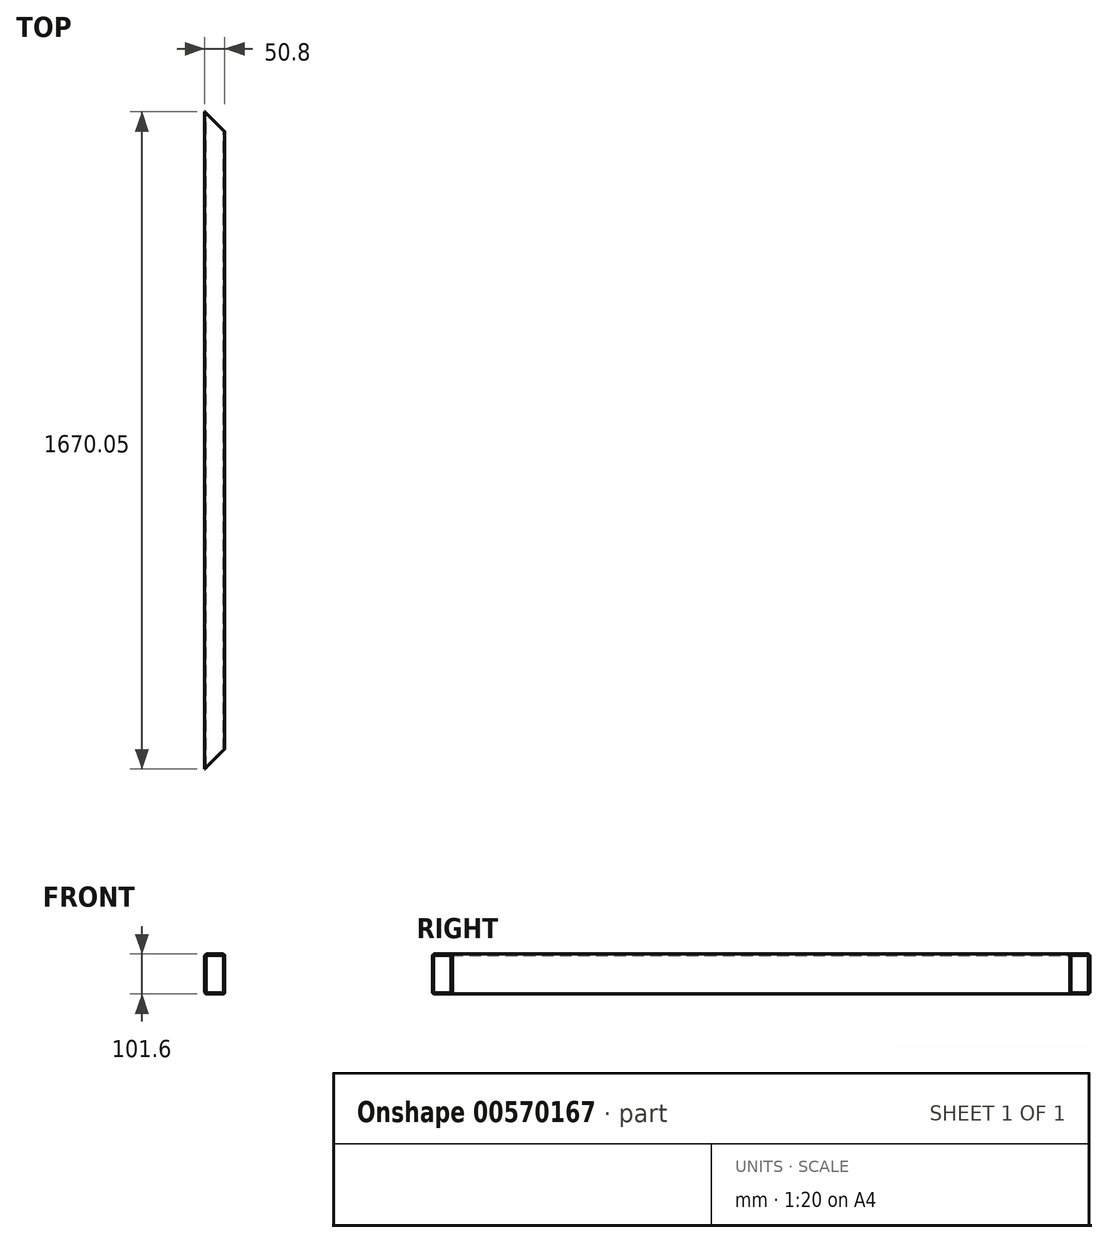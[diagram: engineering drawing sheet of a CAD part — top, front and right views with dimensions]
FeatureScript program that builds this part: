
annotation { "Feature Type Name" : "Feature", "Feature Type Description" : "" }
export const myFeature = defineFeature(function(context is Context, id is Id, definition is map)
    precondition{}
    {
        {
            var Q0;
            Q0=qCreatedBy(makeId("Front.planeOp"),FACE);
            var sketch = newSketch(context, id + "F0", { "sketchPlane" : qUnion([Q0])});
            skLineSegment(sketch, "E0.bottom", {"start": v(0, 0) * mm, "end": v(50.8, 0) * mm});
            skLineSegment(sketch, "E0.top", {"start": v(0, 101.6) * mm, "end": v(50.8, 101.6) * mm});
            skLineSegment(sketch, "E0.left", {"start": v(0, 0) * mm, "end": v(0, 101.6) * mm});
            skLineSegment(sketch, "E0.right", {"start": v(50.8, 0) * mm, "end": v(50.8, 101.6) * mm});
            skLineSegment(sketch, "E1.bottom", {"start": v(3.17, 3.18) * mm, "end": v(47.62, 3.18) * mm});
            skLineSegment(sketch, "E1.top", {"start": v(3.17, 98.43) * mm, "end": v(47.62, 98.43) * mm});
            skLineSegment(sketch, "E1.left", {"start": v(3.17, 3.18) * mm, "end": v(3.17, 98.43) * mm});
            skLineSegment(sketch, "E1.right", {"start": v(47.62, 3.18) * mm, "end": v(47.62, 98.43) * mm});
            skSolve(sketch);
        }
        {
            var Q0;
            Q0=makeQuery(id+"F0.imprint","IMPRINT",FACE,{"disambiguationData":[TD([[makeQuery(id+"F0.imprint","IMPRINT",EDGE,{"derivedFrom":sQuery(id+"F0.wireOp",EDGE,"E0.bottom")}),1.0]])]});
            extrude(context, id + "F1", {"entities" : qUnion([Q0]), "depth" : 1670.05 * mm, "offsetDistance" : 25.4 * mm});
        }
        {
            var Q0;
            Q0=makeQuery(id+"F1.opExtrude","SWEPT_FACE",FACE,{"disambiguationData":[OSD([sQuery(id+"F0.wireOp",EDGE,"E0.top")])]});
            var sketch = newSketch(context, id + "F2", { "sketchPlane" : qUnion([Q0])});
            skLineSegment(sketch, "E2", {"start": v(0, 0) * mm, "end": v(50.8, 0) * mm});
            skLineSegment(sketch, "E3", {"start": v(50.8, 0) * mm, "end": v(50.8, -50.8) * mm});
            skLineSegment(sketch, "E4", {"start": v(50.8, -50.8) * mm, "end": v(0, 0) * mm});
            skLineSegment(sketch, "E5", {"start": v(0, -1670.05) * mm, "end": v(50.8, -1619.25) * mm});
            skLineSegment(sketch, "E6", {"start": v(50.8, -1619.25) * mm, "end": v(50.8, -1670.05) * mm});
            skLineSegment(sketch, "E7", {"start": v(50.8, -1670.05) * mm, "end": v(0, -1670.05) * mm});
            skSolve(sketch);
        }
        {
            var Q0;
            Q0=makeQuery(id+"F2.imprint","IMPRINT",FACE,{"disambiguationData":[TD([[makeQuery(id+"F2.imprint","IMPRINT",EDGE,{"derivedFrom":sQuery(id+"F2.wireOp",EDGE,"E5")}),-1.0]])]});
            var Q1;
            Q1=makeQuery(id+"F2.imprint","IMPRINT",FACE,{"disambiguationData":[TD([[makeQuery(id+"F2.imprint","IMPRINT",EDGE,{"derivedFrom":sQuery(id+"F2.wireOp",EDGE,"E2")}),-1.0]])]});
            extrude(context, id + "F3", {"entities" : qUnion([Q0, Q1]), "operationType" : NewBodyOperationType.REMOVE, "oppositeDirection" : true, "depth" : 228.6 * mm, "offsetDistance" : 25.4 * mm});
        }
        {
            var Q0;
            Q0=makeQuery(id+"F1.opExtrude","SWEPT_EDGE",EDGE,{"disambiguationData":[OSD([sQuery(id+"F0.wireOp",EDGE,"E0.top"),sQuery(id+"F0.wireOp",EDGE,"E0.right")])]});
            var Q1;
            Q1=makeQuery(id+"F1.opExtrude","SWEPT_EDGE",EDGE,{"disambiguationData":[OSD([sQuery(id+"F0.wireOp",EDGE,"E0.bottom"),sQuery(id+"F0.wireOp",EDGE,"E0.right")])]});
            var Q2;
            Q2=makeQuery(id+"F1.opExtrude","SWEPT_EDGE",EDGE,{"disambiguationData":[OSD([sQuery(id+"F0.wireOp",EDGE,"E0.top"),sQuery(id+"F0.wireOp",EDGE,"E0.left")])]});
            var Q3;
            Q3=makeQuery(id+"F1.opExtrude","SWEPT_EDGE",EDGE,{"disambiguationData":[OSD([sQuery(id+"F0.wireOp",EDGE,"E0.bottom"),sQuery(id+"F0.wireOp",EDGE,"E0.left")])]});
            fillet(context, id + "F4", {"entities" : qUnion([Q0, Q1, Q2, Q3]), "radius" : 5.08 * mm, "tangentPropagation" : true, "allowEdgeOverflow" : false});
        }
    });
